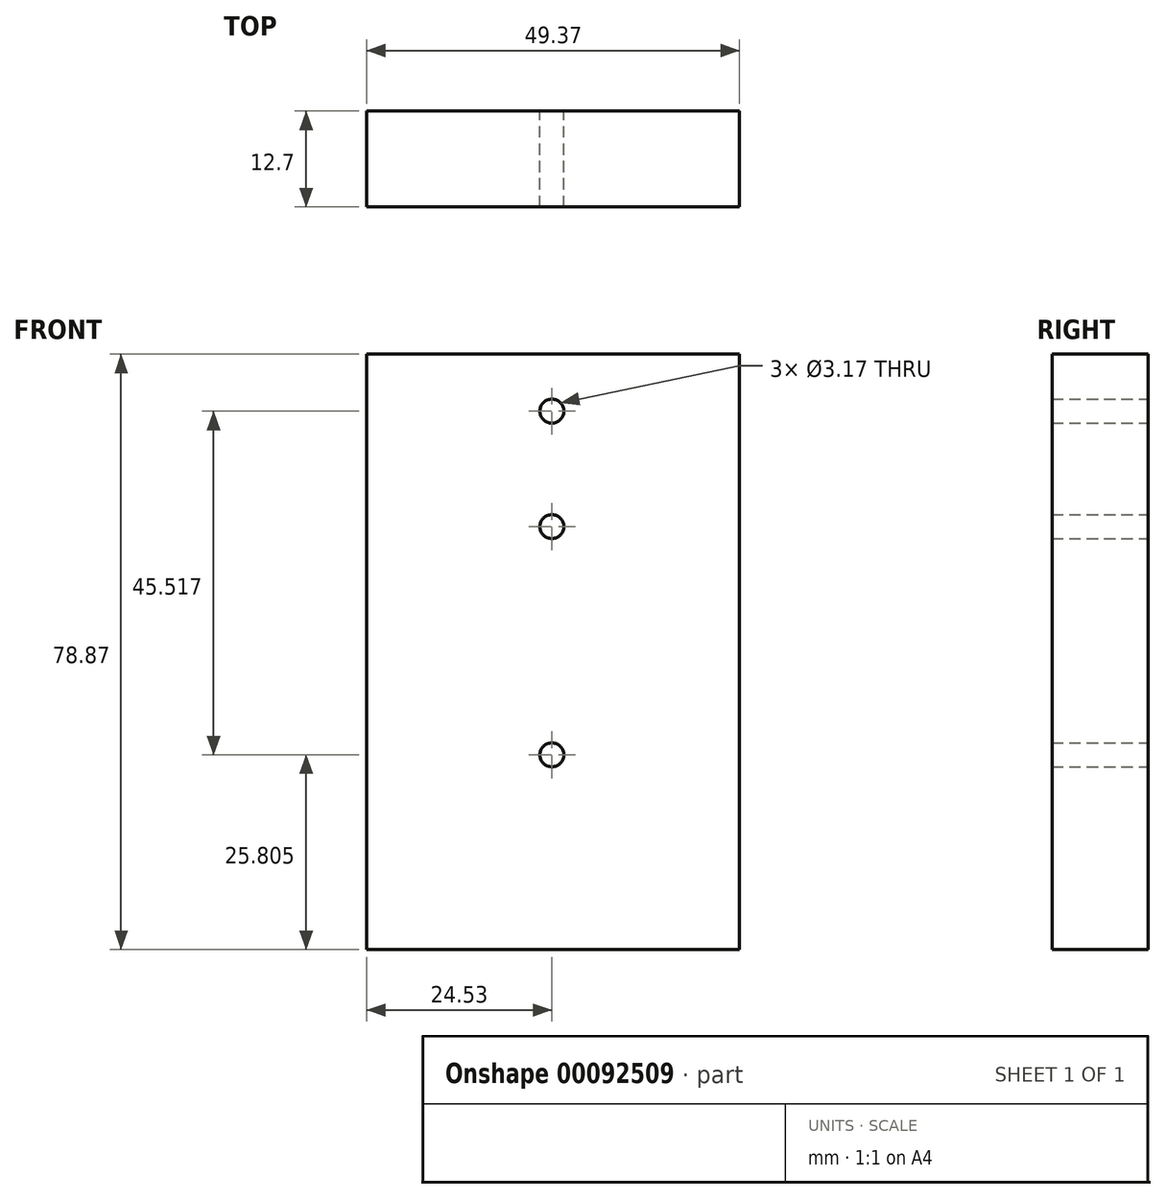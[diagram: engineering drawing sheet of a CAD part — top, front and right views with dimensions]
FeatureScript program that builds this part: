
annotation { "Feature Type Name" : "Feature", "Feature Type Description" : "" }
export const myFeature = defineFeature(function(context is Context, id is Id, definition is map)
    precondition{}
    {
        {
            var Q0;
            Q0=qCreatedBy(makeId("Front.planeOp"),FACE);
            var sketch = newSketch(context, id + "F0", { "sketchPlane" : qUnion([Q0])});
            skLineSegment(sketch, "E0.bottom", {"start": v(-24.53, 45.1) * mm, "end": v(24.84, 45.1) * mm});
            skLineSegment(sketch, "E0.top", {"start": v(-24.53, -33.77) * mm, "end": v(24.84, -33.77) * mm});
            skLineSegment(sketch, "E0.left", {"start": v(-24.53, 45.1) * mm, "end": v(-24.53, -33.77) * mm});
            skLineSegment(sketch, "E0.right", {"start": v(24.84, 45.1) * mm, "end": v(24.84, -33.77) * mm});
            skCircle(sketch, "E1", {"center": v(0, 37.55) * mm, "radius": 1.59 * mm});
            skCircle(sketch, "E2", {"center": v(0, 22.26) * mm, "radius": 1.59 * mm});
            skCircle(sketch, "E3", {"center": v(0, -7.97) * mm, "radius": 1.59 * mm});
            skSolve(sketch);
        }
        {
            var Q0;
            Q0=makeQuery(id+"F0.imprint","IMPRINT",FACE,{"disambiguationData":[TD([[makeQuery(id+"F0.imprint","IMPRINT",EDGE,{"derivedFrom":sQuery(id+"F0.wireOp",EDGE,"E0.bottom")}),-1.0]])]});
            extrude(context, id + "F1", {"entities" : qUnion([Q0]), "depth" : 12.7 * mm});
        }
    });
